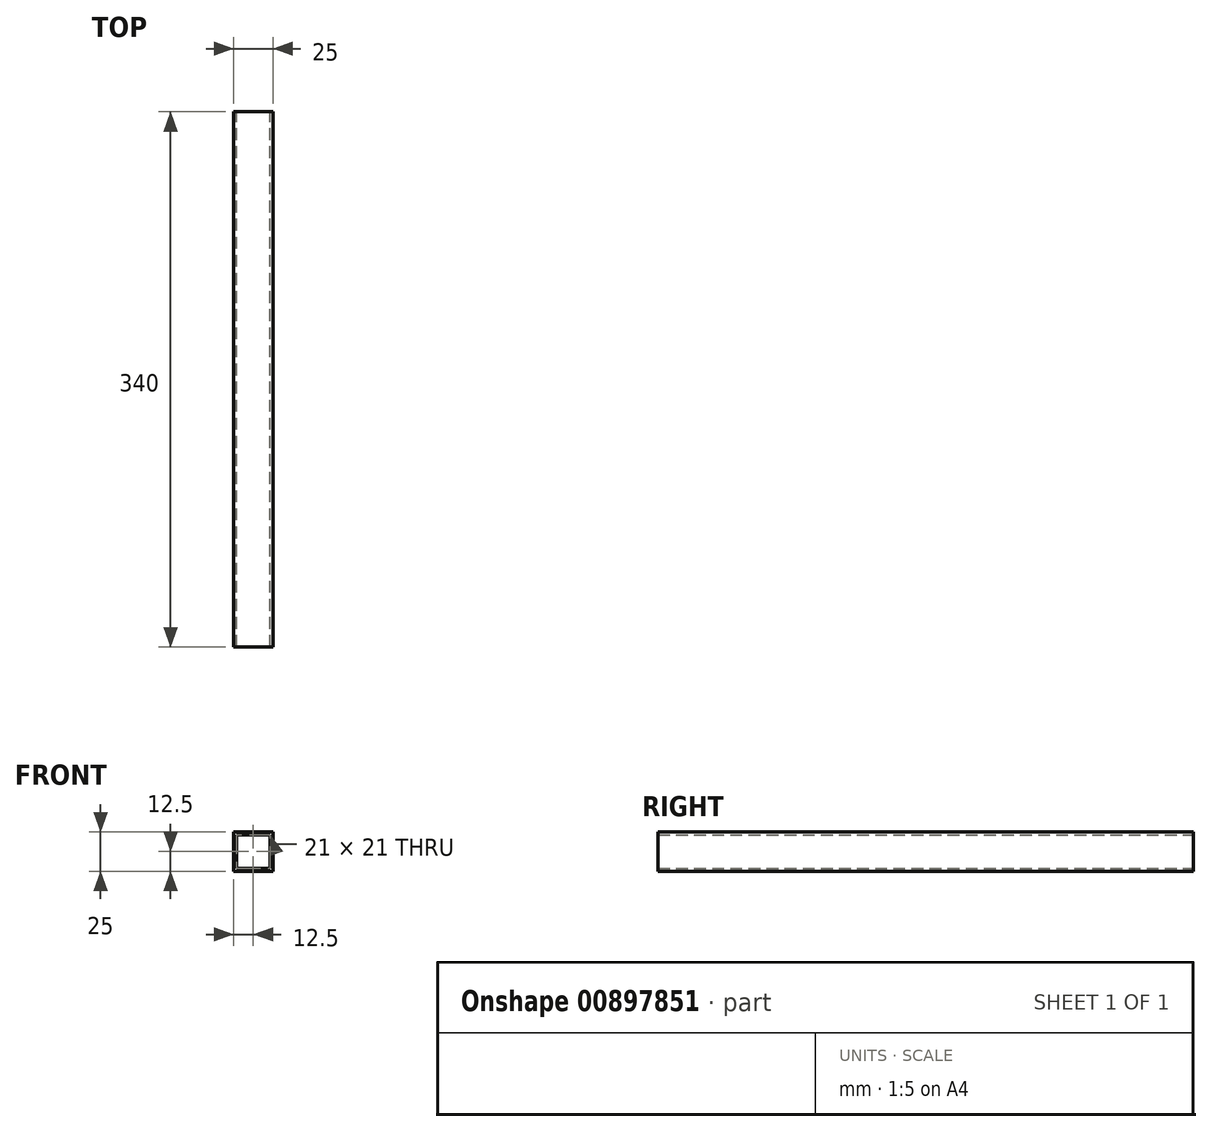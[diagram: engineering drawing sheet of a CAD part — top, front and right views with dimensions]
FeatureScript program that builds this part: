
annotation { "Feature Type Name" : "Feature", "Feature Type Description" : "" }
export const myFeature = defineFeature(function(context is Context, id is Id, definition is map)
    precondition{}
    {
        {
            var Q0;
            Q0=qCreatedBy(makeId("Front.planeOp"),FACE);
            var sketch = newSketch(context, id + "F0", { "sketchPlane" : qUnion([Q0])});
            skLineSegment(sketch, "E0.bottom", {"start": v(12.5, -12.5) * mm, "end": v(-12.5, -12.5) * mm});
            skLineSegment(sketch, "E0.top", {"start": v(12.5, 12.5) * mm, "end": v(-12.5, 12.5) * mm});
            skLineSegment(sketch, "E0.left", {"start": v(12.5, -12.5) * mm, "end": v(12.5, 12.5) * mm});
            skLineSegment(sketch, "E0.right", {"start": v(-12.5, -12.5) * mm, "end": v(-12.5, 12.5) * mm});
            skPoint(sketch, "E0.middle", {"position": v(0, 0) * mm});
            skLineSegment(sketch, "E1.0", {"start": v(10.5, 10.5) * mm, "end": v(-10.5, 10.5) * mm});
            skLineSegment(sketch, "E1.1", {"start": v(10.5, -10.5) * mm, "end": v(10.5, 10.5) * mm});
            skLineSegment(sketch, "E1.2", {"start": v(10.5, -10.5) * mm, "end": v(-10.5, -10.5) * mm});
            skLineSegment(sketch, "E1.3", {"start": v(-10.5, -10.5) * mm, "end": v(-10.5, 10.5) * mm});
            skSolve(sketch);
        }
        {
            var Q0;
            Q0 = qSketchRegion(id + "F0", true);
            extrude(context, id + "F1", {"entities" : qUnion([Q0]), "depth" : 170 * mm, "offsetDistance" : 25 * mm, "hasSecondDirection" : true, "secondDirectionOppositeDirection" : true, "secondDirectionDepth" : 170 * mm});
        }
    });
